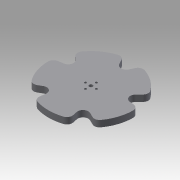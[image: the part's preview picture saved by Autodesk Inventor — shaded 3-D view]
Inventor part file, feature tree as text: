
AUTODESK INVENTOR PART (.ipt)
format: ipt  version: 2016 (Build 200138000, 138)  size: 177,664 bytes
history: native  units: in
note: dims shown in document units (in); Inventor stores cm internally (conversion verified against a paired STEP export)
features: sketch x4, extrude x3, reference x3, fillet x2, pattern_circular x1, hole x1, projected_geometry x1
ambient origin geometry x8: Origin, YZ Plane, XZ Plane, XY Plane, X Axis, Y Axis, Z Axis, Center Point
bodies: Solid1 (feature_tree)
feature tree (15):
  extrude  "Extrusion1"  Depth=0.45in TaperAngle=0.0deg
  extrude  "Extrusion2"  Depth=0.375in
  fillet  "Fillet1"  [1 undecoded]
  fillet  "Fillet2"  Radius=0.375in
  pattern_circular  "Circular Pattern1"  Count=5 Angle=360.0deg
  hole  "Hole1"  [1 undecoded]
  extrude  "Extrusion3"  Depth=0.385in
  sketch  "Sketch1"  dims[d0=6.0in d1=0.45in d2=0.0in]
  sketch  "Sketch2"  dims[d3=0.5in d4=0.75in d5=0.0in d6=0.0in d7=0.375in]
  sketch  "Sketch4"  dims[d8=0.375in d9=1.9685in d10=360.0deg]
  sketch  "Sketch5"  dims[d16=1.25in d19=0.25in d20=0.25in d21=0.75in d22=0.375in d23=0.25in d24=0.5635in d25=1.0in d26=0.8108in d27=0.385in d28=0.1562in d29=1.5748in d31=360.0deg d33=0.5in d34=0.0in]
  projected_geometry  "Projected Loop1"
  reference  "Reference1"
  reference  "Reference2"
  reference  "Reference3"
note: 2 required parameter values undecoded (feature->parameter linkage not recoverable at this tier; creation-order binding heuristic only, values carry confidence <= 0.55)
